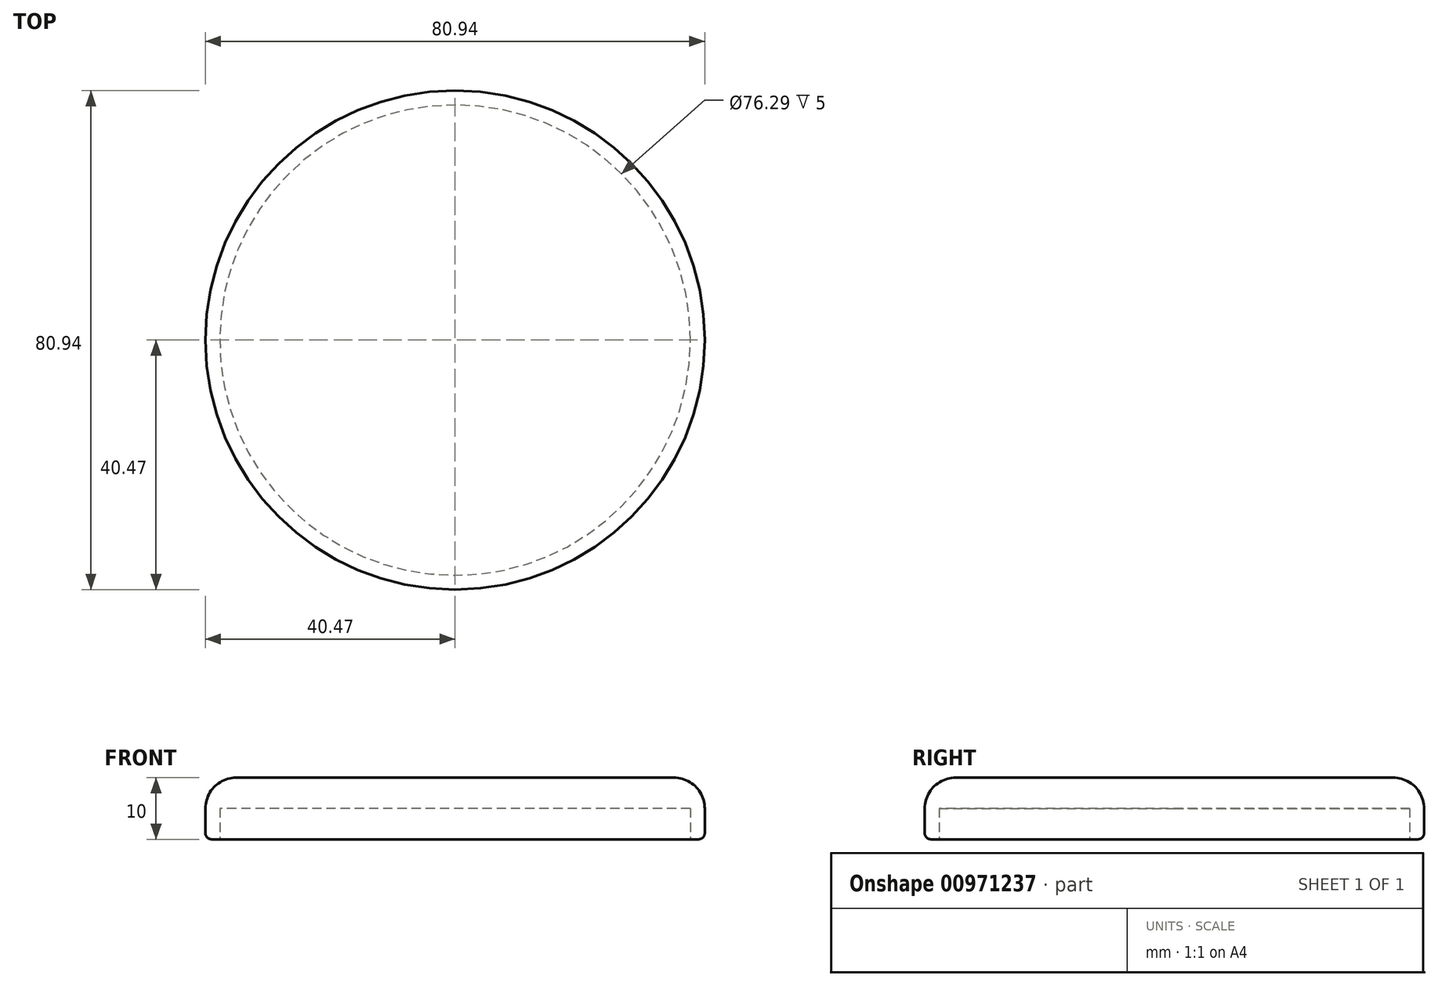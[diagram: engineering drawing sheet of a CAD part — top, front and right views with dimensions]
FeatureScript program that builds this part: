
annotation { "Feature Type Name" : "Feature", "Feature Type Description" : "" }
export const myFeature = defineFeature(function(context is Context, id is Id, definition is map)
    precondition{}
    {
        {
            var Q0;
            Q0=qCreatedBy(makeId("Top.planeOp"),FACE);
            var sketch = newSketch(context, id + "F0", { "sketchPlane" : qUnion([Q0])});
            skCircle(sketch, "E0", {"center": v(0, 0) * mm, "radius": 38.15 * mm});
            skCircle(sketch, "E1", {"center": v(0, 0) * mm, "radius": 40.47 * mm});
            skSolve(sketch);
        }
        {
            var Q0;
            Q0 = qSketchRegion(id + "F0", true);
            extrude(context, id + "F1", {"entities" : qUnion([Q0]), "depth" : 5 * mm, "offsetDistance" : 25 * mm});
        }
        {
            var Q0;
            Q0=makeQuery(id+"F1.opExtrude","CAP_FACE",FACE,{"disambiguationData":[OSD([sQuery(id+"F0.wireOp",EDGE,"E0"),sQuery(id+"F0.wireOp",EDGE,"E1")])],"isStart":false});
            var sketch = newSketch(context, id + "F2", { "sketchPlane" : qUnion([Q0])});
            skCircle(sketch, "E2", {"center": v(0, 0) * mm, "radius": 40.47 * mm});
            skSolve(sketch);
        }
        {
            var Q0;
            Q0 = qSketchRegion(id + "F2", true);
            extrude(context, id + "F3", {"entities" : qUnion([Q0]), "operationType" : NewBodyOperationType.ADD, "depth" : 5 * mm, "offsetDistance" : 25 * mm});
        }
        {
            var Q0;
            Q0=makeQuery(id+"F3.opExtrude","CAP_EDGE",EDGE,{"disambiguationData":[OSD([sQuery(id+"F2.wireOp",EDGE,"E2")])],"isStart":false});
            fillet(context, id + "F4", {"entities" : qUnion([Q0]), "radius" : 5 * mm, "tangentPropagation" : true, "allowEdgeOverflow" : false});
        }
        {
            var Q0;
            Q0=makeQuery(id+"F1.opExtrude","CAP_EDGE",EDGE,{"disambiguationData":[OSD([sQuery(id+"F0.wireOp",EDGE,"E1")])],"isStart":true});
            fillet(context, id + "F5", {"entities" : qUnion([Q0]), "radius" : 1 * mm, "tangentPropagation" : true, "allowEdgeOverflow" : false});
        }
    });
